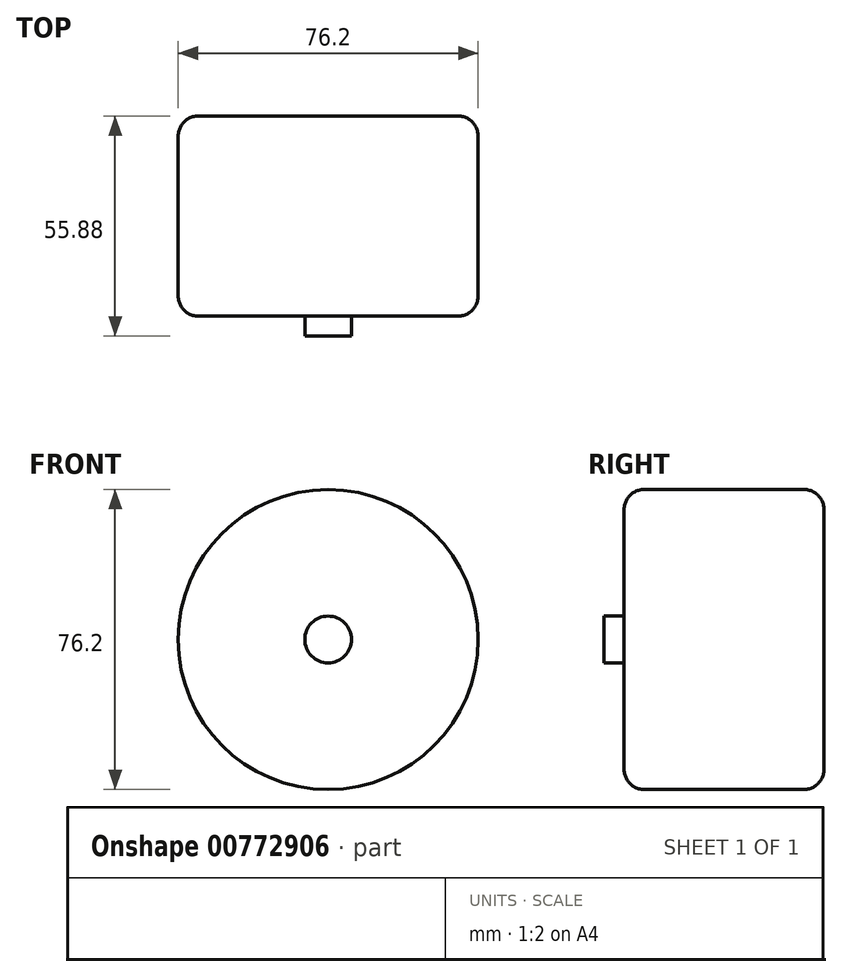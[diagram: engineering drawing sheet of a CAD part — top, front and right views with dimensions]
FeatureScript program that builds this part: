
annotation { "Feature Type Name" : "Feature", "Feature Type Description" : "" }
export const myFeature = defineFeature(function(context is Context, id is Id, definition is map)
    precondition{}
    {
        {
            var Q0;
            Q0=qCreatedBy(makeId("Front.planeOp"),FACE);
            var sketch = newSketch(context, id + "F0", { "sketchPlane" : qUnion([Q0])});
            skCircle(sketch, "E0", {"center": v(0, 0) * mm, "radius": 5.94 * mm});
            skSolve(sketch);
        }
        {
            var Q0;
            Q0=makeQuery(id+"F0.imprint","IMPRINT",FACE,{"disambiguationData":[TD([[makeQuery(id+"F0.imprint","IMPRINT",EDGE,{"derivedFrom":sQuery(id+"F0.wireOp",EDGE,"E0")}),1.0]])]});
            extrude(context, id + "F1", {"entities" : qUnion([Q0]), "depth" : 5.08 * mm, "offsetDistance" : 25.4 * mm});
        }
        {
            var Q0;
            Q0=makeQuery(id+"F1.opExtrude","CAP_FACE",FACE,{"disambiguationData":[OSD([sQuery(id+"F0.wireOp",EDGE,"E0")])],"isStart":true});
            var sketch = newSketch(context, id + "F2", { "sketchPlane" : qUnion([Q0])});
            skCircle(sketch, "E1", {"center": v(0, 0) * mm, "radius": 38.1 * mm});
            skSolve(sketch);
        }
        {
            var Q0;
            Q0 = qSketchRegion(id + "F2", true);
            extrude(context, id + "F3", {"entities" : qUnion([Q0]), "operationType" : NewBodyOperationType.ADD, "depth" : 50.8 * mm, "offsetDistance" : 25.4 * mm});
        }
        {
            var Q0;
            Q0=makeQuery(id+"F3.opExtrude","CAP_EDGE",EDGE,{"disambiguationData":[OSD([sQuery(id+"F2.wireOp",EDGE,"E1")])],"isStart":true});
            var Q1;
            Q1=makeQuery(id+"F3.opExtrude","CAP_EDGE",EDGE,{"disambiguationData":[OSD([sQuery(id+"F2.wireOp",EDGE,"E1")])],"isStart":false});
            fillet(context, id + "F4", {"entities" : qUnion([Q0, Q1]), "radius" : 5.08 * mm, "tangentPropagation" : true, "allowEdgeOverflow" : false});
        }
    });
